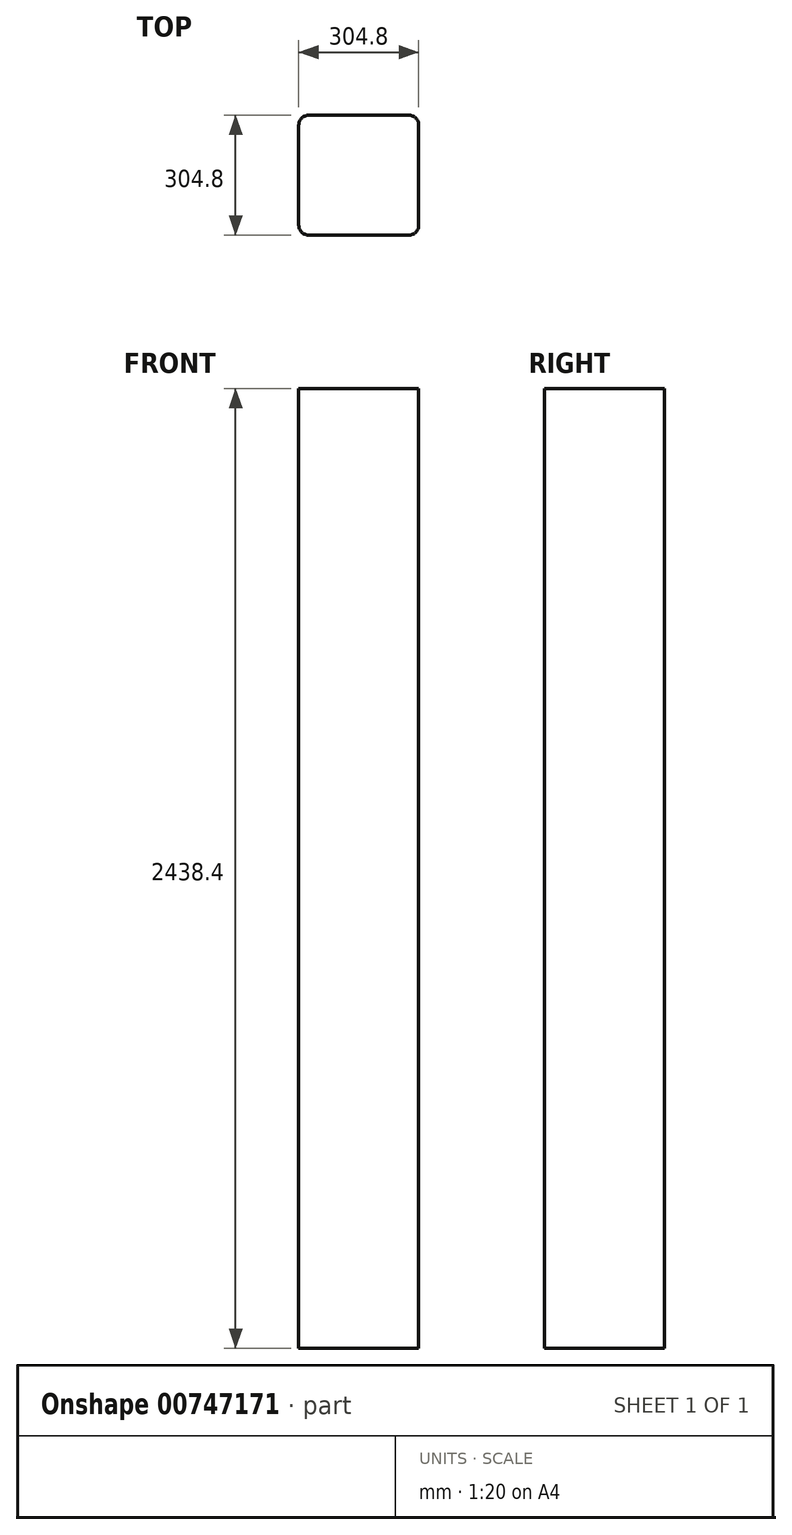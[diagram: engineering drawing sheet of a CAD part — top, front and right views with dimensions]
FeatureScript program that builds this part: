
annotation { "Feature Type Name" : "Feature", "Feature Type Description" : "" }
export const myFeature = defineFeature(function(context is Context, id is Id, definition is map)
    precondition{}
    {
        {
            var Q0;
            Q0=qCreatedBy(makeId("Top.planeOp"),FACE);
            var sketch = newSketch(context, id + "F0", { "sketchPlane" : qUnion([Q0])});
            skLineSegment(sketch, "E0.bottom", {"start": v(0, -159.54) * mm, "end": v(304.8, -159.54) * mm});
            skLineSegment(sketch, "E0.top", {"start": v(0, -464.34) * mm, "end": v(304.8, -464.34) * mm});
            skLineSegment(sketch, "E0.left", {"start": v(0, -159.54) * mm, "end": v(0, -464.34) * mm});
            skLineSegment(sketch, "E0.right", {"start": v(304.8, -159.54) * mm, "end": v(304.8, -464.34) * mm});
            skSolve(sketch);
        }
        {
            var Q0;
            Q0 = qSketchRegion(id + "F0", true);
            extrude(context, id + "F1", {"entities" : qUnion([Q0]), "depth" : 2438.4 * mm, "offsetDistance" : 25.4 * mm});
        }
        {
            var Q0;
            Q0=makeQuery(id+"F1.opExtrude","SWEPT_EDGE",EDGE,{"disambiguationData":[OSD([sQuery(id+"F0.wireOp",EDGE,"E0.top"),sQuery(id+"F0.wireOp",EDGE,"E0.left")])]});
            var Q1;
            Q1=makeQuery(id+"F1.opExtrude","SWEPT_EDGE",EDGE,{"disambiguationData":[OSD([sQuery(id+"F0.wireOp",EDGE,"E0.bottom"),sQuery(id+"F0.wireOp",EDGE,"E0.right")])]});
            var Q2;
            Q2=makeQuery(id+"F1.opExtrude","SWEPT_EDGE",EDGE,{"disambiguationData":[OSD([sQuery(id+"F0.wireOp",EDGE,"E0.bottom"),sQuery(id+"F0.wireOp",EDGE,"E0.left")])]});
            var Q3;
            Q3=makeQuery(id+"F1.opExtrude","SWEPT_EDGE",EDGE,{"disambiguationData":[OSD([sQuery(id+"F0.wireOp",EDGE,"E0.top"),sQuery(id+"F0.wireOp",EDGE,"E0.right")])]});
            fillet(context, id + "F2", {"entities" : qUnion([Q0, Q1, Q2, Q3]), "radius" : 25.4 * mm, "tangentPropagation" : true, "allowEdgeOverflow" : false});
        }
    });
